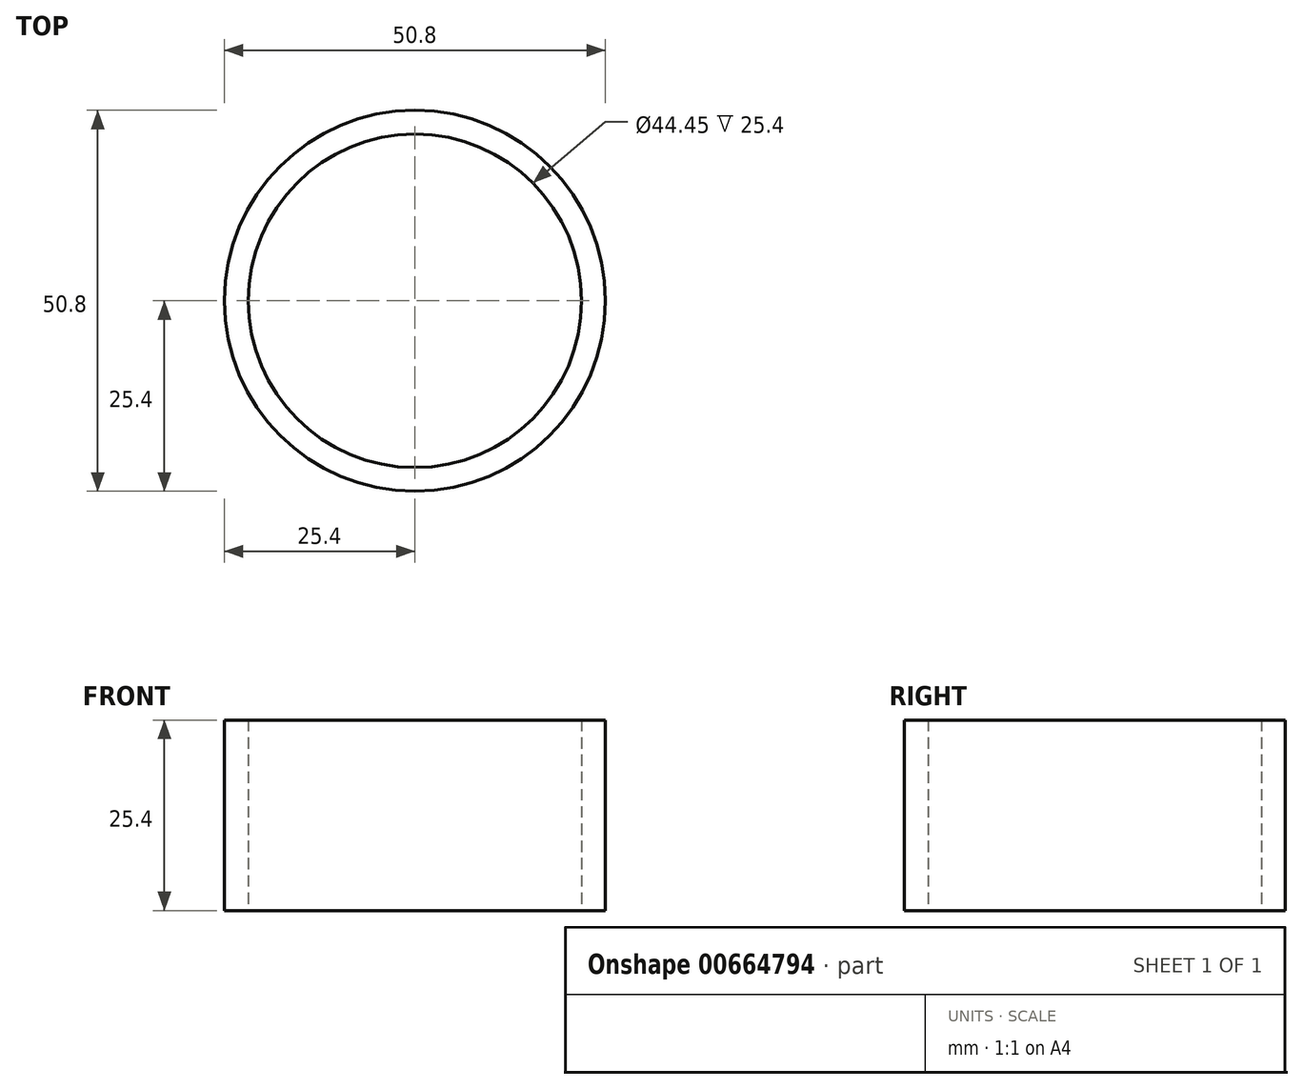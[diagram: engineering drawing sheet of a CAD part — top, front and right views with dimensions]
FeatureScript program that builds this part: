
annotation { "Feature Type Name" : "Feature", "Feature Type Description" : "" }
export const myFeature = defineFeature(function(context is Context, id is Id, definition is map)
    precondition{}
    {
        {
            var Q0;
            Q0=qCreatedBy(makeId("Top.planeOp"),FACE);
            var sketch = newSketch(context, id + "F0", { "sketchPlane" : qUnion([Q0])});
            skCircle(sketch, "E0", {"center": v(0, 0) * mm, "radius": 25.4 * mm});
            skCircle(sketch, "E1", {"center": v(0, 0) * mm, "radius": 22.23 * mm});
            skCircle(sketch, "E2", {"center": v(0, 0) * mm, "radius": 2.54 * mm});
            skLineSegment(sketch, "E3", {"start": v(0, 2.54) * mm, "end": v(-5.84, 21.45) * mm});
            skLineSegment(sketch, "E4", {"start": v(0, 2.54) * mm, "end": v(6.73, 21.18) * mm});
            skSolve(sketch);
        }
        {
            var Q0;
            Q0=makeQuery(id+"F0.imprint","IMPRINT",FACE,{"disambiguationData":[TD([[makeQuery(id+"F0.imprint","IMPRINT",EDGE,{"derivedFrom":sQuery(id+"F0.wireOp",EDGE,"E0")}),1.0]])]});
            extrude(context, id + "F1", {"entities" : qUnion([Q0]), "depth" : 25.4 * mm, "offsetDistance" : 25.4 * mm});
        }
    });
